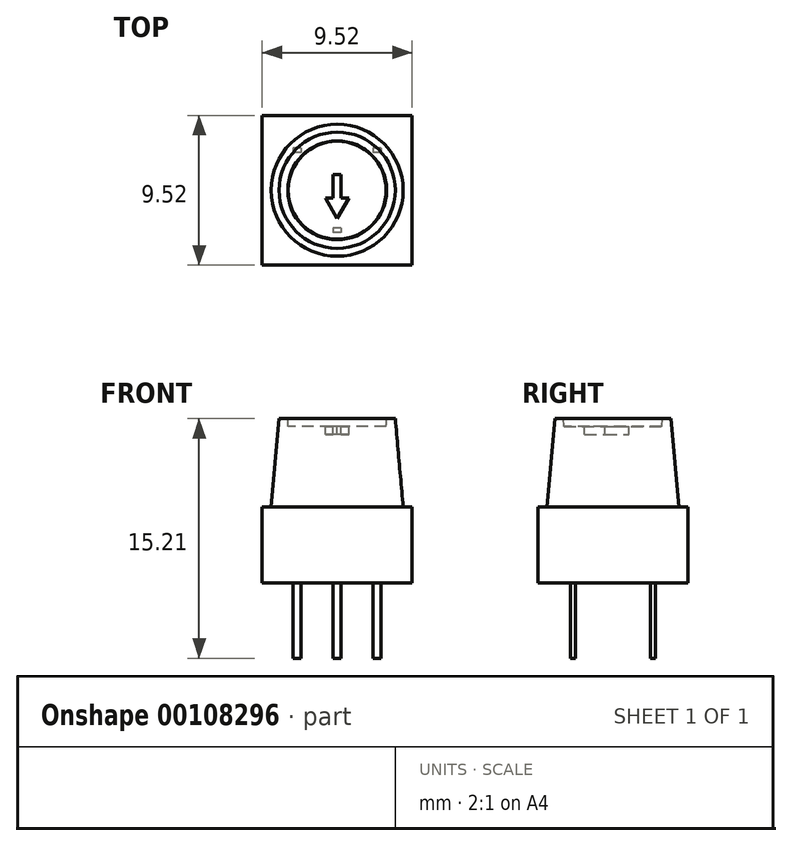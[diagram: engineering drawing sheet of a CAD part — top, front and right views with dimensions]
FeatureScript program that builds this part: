
annotation { "Feature Type Name" : "Feature", "Feature Type Description" : "" }
export const myFeature = defineFeature(function(context is Context, id is Id, definition is map)
    precondition{}
    {
        {
            var Q0;
            Q0=qCreatedBy(makeId("Top.planeOp"),FACE);
            var sketch = newSketch(context, id + "F0", { "sketchPlane" : qUnion([Q0])});
            skLineSegment(sketch, "E0.bottom", {"start": v(4.76, -4.76) * mm, "end": v(-4.76, -4.76) * mm});
            skLineSegment(sketch, "E0.top", {"start": v(4.76, 4.76) * mm, "end": v(-4.76, 4.76) * mm});
            skLineSegment(sketch, "E0.left", {"start": v(4.76, -4.76) * mm, "end": v(4.76, 4.76) * mm});
            skLineSegment(sketch, "E0.right", {"start": v(-4.76, -4.76) * mm, "end": v(-4.76, 4.76) * mm});
            skPoint(sketch, "E0.middle", {"position": v(0, 0) * mm});
            skSolve(sketch);
        }
        {
            var Q0;
            Q0=makeQuery(id+"F0.imprint","IMPRINT",FACE,{"disambiguationData":[TD([[makeQuery(id+"F0.imprint","IMPRINT",EDGE,{"derivedFrom":sQuery(id+"F0.wireOp",EDGE,"E0.bottom")}),-1.0]])]});
            extrude(context, id + "F1", {"entities" : qUnion([Q0]), "depth" : 4.83 * mm});
        }
        {
            var Q0;
            Q0=makeQuery(id+"F1.opExtrude","CAP_FACE",FACE,{"disambiguationData":[OSD([sQuery(id+"F0.wireOp",EDGE,"E0.bottom"),sQuery(id+"F0.wireOp",EDGE,"E0.top"),sQuery(id+"F0.wireOp",EDGE,"E0.left"),sQuery(id+"F0.wireOp",EDGE,"E0.right")])],"isStart":false});
            cPlane(context, id + "F2", {"entities" : qUnion([Q0]), "cplaneType" : CPlaneType.OFFSET, "offset" : 0 * mm, "width" : 152.4 * mm, "height" : 152.4 * mm});
        }
        {
            var Q0;
            Q0=makeQuery(id+"F1.opExtrude","CAP_FACE",FACE,{"disambiguationData":[OSD([sQuery(id+"F0.wireOp",EDGE,"E0.bottom"),sQuery(id+"F0.wireOp",EDGE,"E0.top"),sQuery(id+"F0.wireOp",EDGE,"E0.left"),sQuery(id+"F0.wireOp",EDGE,"E0.right")])],"isStart":false});
            var sketch = newSketch(context, id + "F3", { "sketchPlane" : qUnion([Q0])});
            skSolve(sketch);
        }
        {
            var Q0;
            Q0=qCreatedBy(id+"F2.planeOp",FACE);
            var sketch = newSketch(context, id + "F4", { "sketchPlane" : qUnion([Q0])});
            skCircle(sketch, "E1", {"center": v(0, 0) * mm, "radius": 4.2 * mm});
            skSolve(sketch);
        }
        {
            var Q0;
            Q0=makeQuery(id+"F3.imprint","IMPRINT",FACE,{"disambiguationData":[TD([[makeQuery(id+"F3.imprint","IMPRINT",EDGE,{"derivedFrom":makeQuery(id+"F1.opExtrude","CAP_EDGE",EDGE,{"disambiguationData":[OSD([sQuery(id+"F0.wireOp",EDGE,"E0.bottom")])],"isStart":false})}),-1.0]])]});
            cPlane(context, id + "F5", {"entities" : qUnion([Q0]), "cplaneType" : CPlaneType.OFFSET, "offset" : 5.6 * mm, "width" : 150 * mm, "height" : 150 * mm});
        }
        {
            var Q0;
            Q0=qCreatedBy(id+"F5.planeOp",FACE);
            var sketch = newSketch(context, id + "F11", { "sketchPlane" : qUnion([Q0])});
            skCircle(sketch, "E2.0", {"center": v(0, 0) * mm, "radius": 4.2 * mm});
            skCircle(sketch, "E3.0", {"center": v(0, 0) * mm, "radius": 3.69 * mm});
            skSolve(sketch);
        }
        {
            var Q0;
            Q0=makeQuery(id+"F4.imprint","IMPRINT",FACE,{"disambiguationData":[TD([[makeQuery(id+"F4.imprint","IMPRINT",EDGE,{"derivedFrom":sQuery(id+"F4.wireOp",EDGE,"E1")}),1.0]])]});
            var Q1;
            Q1=makeQuery(id+"F11.imprint","IMPRINT",FACE,{"disambiguationData":[TD([[makeQuery(id+"F11.imprint","IMPRINT",EDGE,{"derivedFrom":sQuery(id+"F11.wireOp",EDGE,"E3.0")}),1.0]])]});
            var Q2;
            Q2=sQuery(id+"F4.wireOp",EDGE,"E1");
            var Q3;
            Q3=sQuery(id+"F11.wireOp",EDGE,"E3.0");
            loft(context, id + "F6", {"sheetProfilesArray" : [{ "sheetProfileEntities" : qUnion([Q0]) }, { "sheetProfileEntities" : qUnion([Q1]) }], "wireProfilesArray" : [{ "wireProfileEntities" : qUnion([Q2]) }, { "wireProfileEntities" : qUnion([Q3]) }]});
        }
        {
            var Q0;
            Q0=makeQuery(id+"F11.imprint","IMPRINT",FACE,{"disambiguationData":[TD([[makeQuery(id+"F11.imprint","IMPRINT",EDGE,{"derivedFrom":sQuery(id+"F11.wireOp",EDGE,"E3.0")}),1.0]])]});
            cPlane(context, id + "F7", {"entities" : qUnion([Q0]), "cplaneType" : CPlaneType.OFFSET, "offset" : 1 * mm, "width" : 150 * mm, "height" : 150 * mm});
        }
        {
            var Q0;
            Q0=qCreatedBy(id+"F7.planeOp",FACE);
            var sketch = newSketch(context, id + "F12", { "sketchPlane" : qUnion([Q0])});
            skCircle(sketch, "E4.0", {"center": v(0, 0) * mm, "radius": 3.69 * mm});
            skCircle(sketch, "E5.0", {"center": v(0, 0) * mm, "radius": 3.19 * mm});
            skLineSegment(sketch, "E6.bottom", {"start": v(0, 0) * mm, "end": v(0, 0) * mm});
            skLineSegment(sketch, "E6.top", {"start": v(0, 0) * mm, "end": v(0, 0) * mm});
            skLineSegment(sketch, "E6.left", {"start": v(0, 0) * mm, "end": v(0, 0) * mm});
            skLineSegment(sketch, "E6.right", {"start": v(0, 0) * mm, "end": v(0, 0) * mm});
            skLineSegment(sketch, "E7.bottom", {"start": v(0.25, -1) * mm, "end": v(-0.25, -1) * mm});
            skLineSegment(sketch, "E7.top", {"start": v(0.25, 1) * mm, "end": v(-0.25, 1) * mm});
            skLineSegment(sketch, "E7.left", {"start": v(0.25, -1) * mm, "end": v(0.25, 1) * mm});
            skLineSegment(sketch, "E7.right", {"start": v(-0.25, -1) * mm, "end": v(-0.25, 1) * mm});
            skLineSegment(sketch, "E8", {"start": v(-0.75, -0.5) * mm, "end": v(0.75, -0.5) * mm});
            skLineSegment(sketch, "E9", {"start": v(0.75, -0.5) * mm, "end": v(0, -1.8) * mm});
            skLineSegment(sketch, "E10", {"start": v(0, -1.8) * mm, "end": v(-0.75, -0.5) * mm});
            skSolve(sketch);
        }
        {
            var Q0;
            Q0=makeQuery(id+"F12.imprint","IMPRINT",FACE,{"disambiguationData":[TD([[makeQuery(id+"F12.imprint","IMPRINT",EDGE,{"derivedFrom":sQuery(id+"F12.wireOp",EDGE,"E5.0")}),1.0]])]});
            var Q1;
            {var subQ0=sQuery(id+"F12.wireOp",EDGE,"E7.top");Q1=makeQuery(id+"F12.imprint","IMPRINT",FACE,{"disambiguationData":[TD([[makeQuery(id+"F12.imprint","IMPRINT",EDGE,{"derivedFrom":subQ0}),1.0]])]});}
            var Q2;
            {var subQ4=sQuery(id+"F12.wireOp",EDGE,"E7.bottom");Q2=makeQuery(id+"F12.imprint","IMPRINT",FACE,{"disambiguationData":[TD([[makeQuery(id+"F12.imprint","IMPRINT",EDGE,{"derivedFrom":subQ4}),1.0]])]});}
            var Q3;
            {var subQ0=sQuery(id+"F12.wireOp",EDGE,"E7.bottom");Q3=makeQuery(id+"F12.imprint","IMPRINT",FACE,{"disambiguationData":[TD([[makeQuery(id+"F12.imprint","IMPRINT",EDGE,{"derivedFrom":subQ0}),-1.0]])]});}
            extrude(context, id + "F8", {"entities" : qUnion([Q0, Q1, Q2, Q3]), "operationType" : NewBodyOperationType.REMOVE, "oppositeDirection" : true, "depth" : 1.5 * mm, "hasDraft" : true, "draftAngle" : 3 * degree, "draftPullDirection" : true});
        }
        {
            var Q0;
            {var subQ4=sQuery(id+"F12.wireOp",EDGE,"E7.bottom");Q0=makeQuery(id+"F12.imprint","IMPRINT",FACE,{"disambiguationData":[TD([[makeQuery(id+"F12.imprint","IMPRINT",EDGE,{"derivedFrom":subQ4}),1.0]])]});}
            var Q1;
            {var subQ0=sQuery(id+"F12.wireOp",EDGE,"E7.top");Q1=makeQuery(id+"F12.imprint","IMPRINT",FACE,{"disambiguationData":[TD([[makeQuery(id+"F12.imprint","IMPRINT",EDGE,{"derivedFrom":subQ0}),1.0]])]});}
            var Q2;
            {var subQ0=sQuery(id+"F12.wireOp",EDGE,"E7.bottom");Q2=makeQuery(id+"F12.imprint","IMPRINT",FACE,{"disambiguationData":[TD([[makeQuery(id+"F12.imprint","IMPRINT",EDGE,{"derivedFrom":subQ0}),-1.0]])]});}
            extrude(context, id + "F13", {"entities" : qUnion([Q0, Q1, Q2]), "operationType" : NewBodyOperationType.REMOVE, "oppositeDirection" : true, "depth" : 2 * mm});
        }
        {
            var Q0;
            Q0=makeQuery(id+"F1.opExtrude","CAP_FACE",FACE,{"disambiguationData":[OSD([sQuery(id+"F0.wireOp",EDGE,"E0.bottom"),sQuery(id+"F0.wireOp",EDGE,"E0.top"),sQuery(id+"F0.wireOp",EDGE,"E0.left"),sQuery(id+"F0.wireOp",EDGE,"E0.right")])],"isStart":true});
            var sketch = newSketch(context, id + "F9", { "sketchPlane" : qUnion([Q0])});
            skLineSegment(sketch, "E11.bottom", {"start": v(0.25, 2.4) * mm, "end": v(-0.26, 2.4) * mm});
            skLineSegment(sketch, "E11.top", {"start": v(0.25, 2.69) * mm, "end": v(-0.26, 2.69) * mm});
            skLineSegment(sketch, "E11.left", {"start": v(0.25, 2.4) * mm, "end": v(0.25, 2.69) * mm});
            skLineSegment(sketch, "E11.right", {"start": v(-0.26, 2.4) * mm, "end": v(-0.26, 2.69) * mm});
            skPoint(sketch, "E11.middle", {"position": v(0, 2.54) * mm});
            skLineSegment(sketch, "E12.bottom", {"start": v(-2.29, -2.7) * mm, "end": v(-2.8, -2.7) * mm});
            skLineSegment(sketch, "E12.top", {"start": v(-2.29, -2.4) * mm, "end": v(-2.8, -2.4) * mm});
            skLineSegment(sketch, "E12.left", {"start": v(-2.29, -2.7) * mm, "end": v(-2.29, -2.4) * mm});
            skLineSegment(sketch, "E12.right", {"start": v(-2.8, -2.7) * mm, "end": v(-2.8, -2.4) * mm});
            skPoint(sketch, "E12.middle", {"position": v(-2.54, -2.54) * mm});
            skLineSegment(sketch, "E13.bottom", {"start": v(2.8, -2.69) * mm, "end": v(2.28, -2.69) * mm});
            skLineSegment(sketch, "E13.top", {"start": v(2.8, -2.4) * mm, "end": v(2.28, -2.4) * mm});
            skLineSegment(sketch, "E13.left", {"start": v(2.8, -2.69) * mm, "end": v(2.8, -2.4) * mm});
            skLineSegment(sketch, "E13.right", {"start": v(2.28, -2.69) * mm, "end": v(2.28, -2.4) * mm});
            skPoint(sketch, "E13.middle", {"position": v(2.54, -2.54) * mm});
            skSolve(sketch);
        }
        {
            var Q0;
            Q0=makeQuery(id+"F9.imprint","IMPRINT",FACE,{"disambiguationData":[TD([[makeQuery(id+"F9.imprint","IMPRINT",EDGE,{"derivedFrom":sQuery(id+"F9.wireOp",EDGE,"E12.bottom")}),-1.0]])]});
            var Q1;
            Q1=makeQuery(id+"F9.imprint","IMPRINT",FACE,{"disambiguationData":[TD([[makeQuery(id+"F9.imprint","IMPRINT",EDGE,{"derivedFrom":sQuery(id+"F9.wireOp",EDGE,"E13.bottom")}),-1.0]])]});
            var Q2;
            Q2=makeQuery(id+"F9.imprint","IMPRINT",FACE,{"disambiguationData":[TD([[makeQuery(id+"F9.imprint","IMPRINT",EDGE,{"derivedFrom":sQuery(id+"F9.wireOp",EDGE,"E11.bottom")}),-1.0]])]});
            extrude(context, id + "F10", {"entities" : qUnion([Q0, Q1, Q2]), "depth" : 4.78 * mm});
        }
    });
